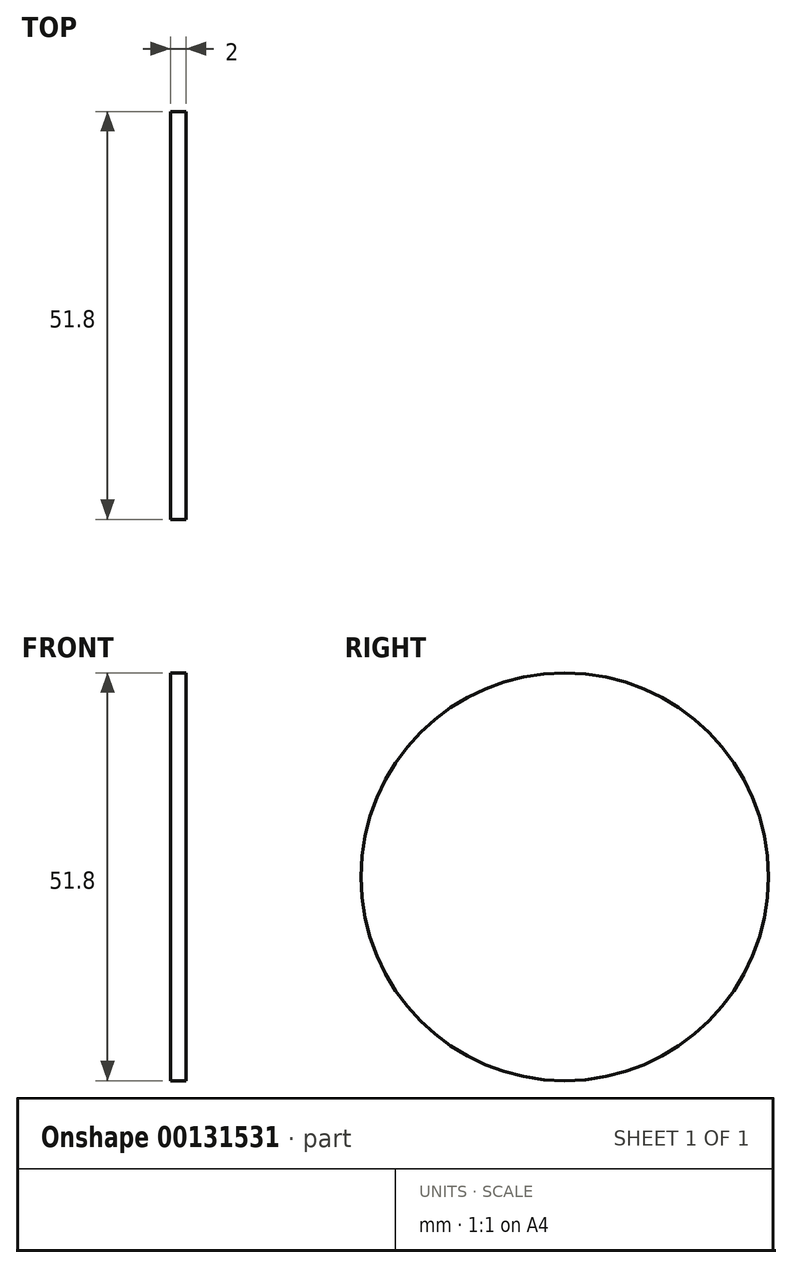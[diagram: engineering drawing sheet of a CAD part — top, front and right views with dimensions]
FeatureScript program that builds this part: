
annotation { "Feature Type Name" : "Feature", "Feature Type Description" : "" }
export const myFeature = defineFeature(function(context is Context, id is Id, definition is map)
    precondition{}
    {
        {
            var Q0;
            Q0=qCreatedBy(makeId("Right.planeOp"),FACE);
            var sketch = newSketch(context, id + "F0", { "sketchPlane" : qUnion([Q0])});
            skCircle(sketch, "E0", {"center": v(0, 0) * mm, "radius": 25.9 * mm});
            skSolve(sketch);
        }
        {
            var Q0;
            Q0=makeQuery(id+"F0.imprint","IMPRINT",FACE,{"disambiguationData":[TD([[makeQuery(id+"F0.imprint","IMPRINT",EDGE,{"derivedFrom":sQuery(id+"F0.wireOp",EDGE,"E0")}),1.0]])]});
            extrude(context, id + "F1", {"entities" : qUnion([Q0]), "depth" : 2 * mm});
        }
    });
